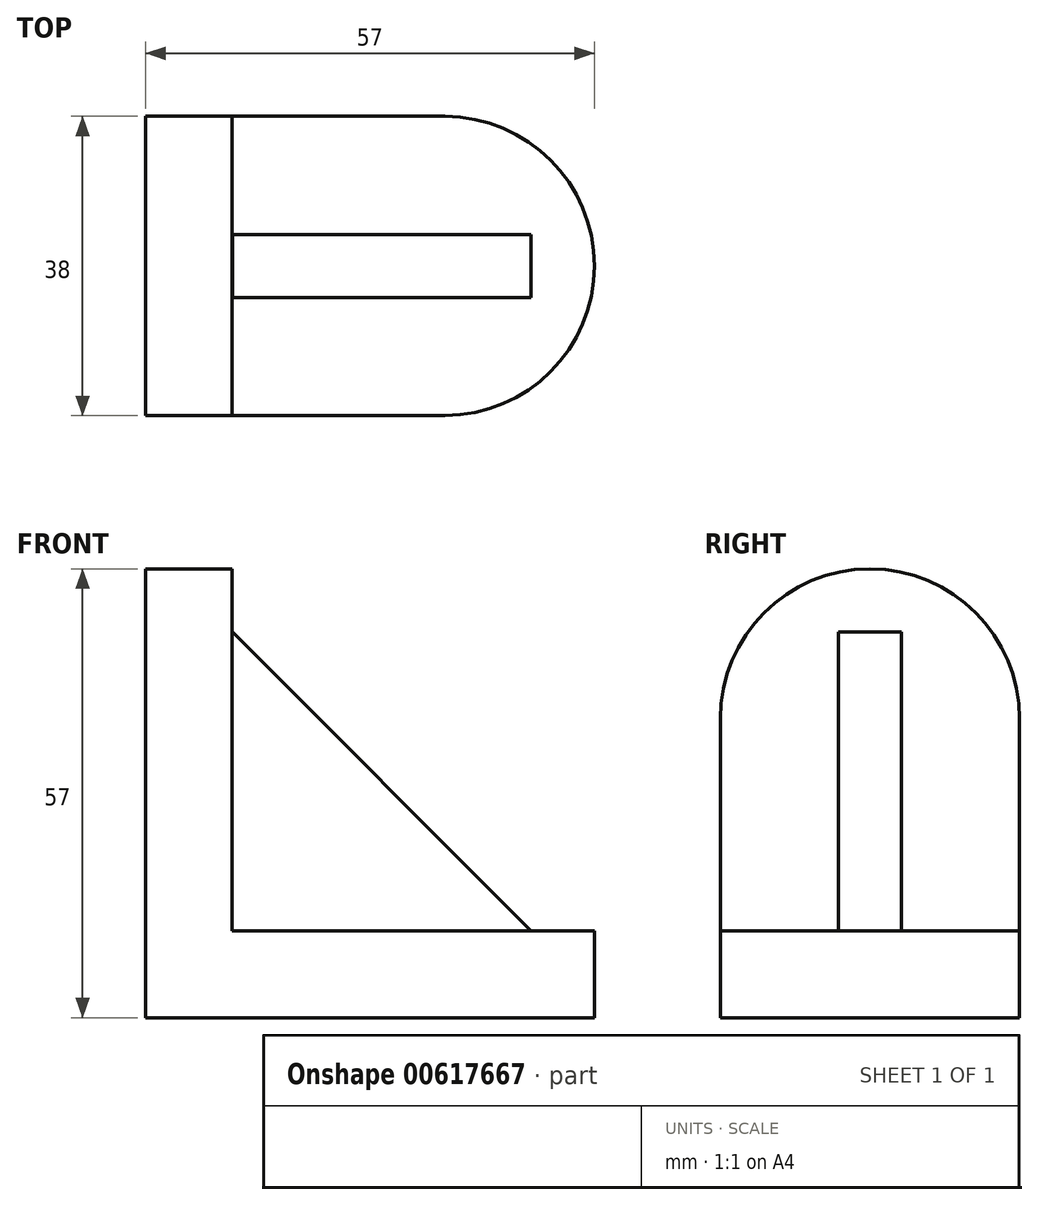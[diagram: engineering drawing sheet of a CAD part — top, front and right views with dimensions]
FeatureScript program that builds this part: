
annotation { "Feature Type Name" : "Feature", "Feature Type Description" : "" }
export const myFeature = defineFeature(function(context is Context, id is Id, definition is map)
    precondition{}
    {
        {
            var Q0;
            Q0=qCreatedBy(makeId("Top.planeOp"),FACE);
            var sketch = newSketch(context, id + "F0", { "sketchPlane" : qUnion([Q0])});
            skLineSegment(sketch, "E0", {"start": v(0, 0) * mm, "end": v(38, 0) * mm});
            skLineSegment(sketch, "E1", {"start": v(38, 38) * mm, "end": v(0, 38) * mm});
            skLineSegment(sketch, "E2", {"start": v(0, 38) * mm, "end": v(0, 0) * mm});
            skArc(sketch, "E3", {"start": v(38, 0) * mm, "mid": v(57, 19) * mm, "end": v(38, 38) * mm});
            skSolve(sketch);
        }
        {
            var Q0;
            Q0=qCreatedBy(makeId("Right.planeOp"),FACE);
            var sketch = newSketch(context, id + "F1", { "sketchPlane" : qUnion([Q0])});
            skLineSegment(sketch, "E4.bottom", {"start": v(0, 0) * mm, "end": v(38, 0) * mm});
            skLineSegment(sketch, "E4.top", {"start": v(0, 38) * mm, "end": v(38, 38) * mm});
            skLineSegment(sketch, "E4.left", {"start": v(0, 0) * mm, "end": v(0, 38) * mm});
            skLineSegment(sketch, "E4.right", {"start": v(38, 0) * mm, "end": v(38, 38) * mm});
            skArc(sketch, "E5", {"start": v(38, 38) * mm, "mid": v(19, 57) * mm, "end": v(0, 38) * mm});
            skSolve(sketch);
        }
        {
            var Q0;
            Q0=makeQuery(id+"F1.imprint","IMPRINT",FACE,{"disambiguationData":[TD([[makeQuery(id+"F1.imprint","IMPRINT",EDGE,{"derivedFrom":sQuery(id+"F1.wireOp",EDGE,"E4.bottom")}),1.0]])]});
            var Q1;
            Q1=makeQuery(id+"F1.imprint","IMPRINT",FACE,{"disambiguationData":[TD([[makeQuery(id+"F1.imprint","IMPRINT",EDGE,{"derivedFrom":sQuery(id+"F1.wireOp",EDGE,"E4.top")}),1.0]])]});
            extrude(context, id + "F2", {"entities" : qUnion([Q0, Q1]), "depth" : 11 * mm, "offsetDistance" : 25.4 * mm});
        }
        {
            var Q0;
            Q0=makeQuery(id+"F0.imprint","IMPRINT",FACE,{"disambiguationData":[TD([[makeQuery(id+"F0.imprint","IMPRINT",EDGE,{"derivedFrom":sQuery(id+"F0.wireOp",EDGE,"E0")}),1.0]])]});
            extrude(context, id + "F3", {"entities" : qUnion([Q0]), "operationType" : NewBodyOperationType.ADD, "depth" : 11 * mm, "offsetDistance" : 25.4 * mm});
        }
        {
            var Q0;
            Q0=makeQuery(id+"F3.opExtrude","CAP_EDGE",EDGE,{"disambiguationData":[OSD([sQuery(id+"F0.wireOp",EDGE,"E3")])],"isStart":false});
            cPoint(context, id + "F4", {"entities" : qUnion([Q0]), "parameter" : 0.5});
        }
        {
            var Q0;
            Q0=makeQuery(id+"F3.boolean.opBoolean","INTERSECT",EDGE,{"derivedFrom":[makeQuery(id+"F2.opExtrude","CAP_FACE",FACE,{"disambiguationData":[OSD([sQuery(id+"F1.wireOp",EDGE,"E4.bottom"),sQuery(id+"F1.wireOp",EDGE,"E4.left"),sQuery(id+"F1.wireOp",EDGE,"E4.right"),sQuery(id+"F1.wireOp",EDGE,"E5")])],"isStart":false}),makeQuery(id+"F3.opExtrude","CAP_FACE",FACE,{"disambiguationData":[OSD([sQuery(id+"F0.wireOp",EDGE,"E0"),sQuery(id+"F0.wireOp",EDGE,"E1"),sQuery(id+"F0.wireOp",EDGE,"E2"),sQuery(id+"F0.wireOp",EDGE,"E3")])],"isStart":false})]});
            cPoint(context, id + "F5", {"entities" : qUnion([Q0]), "parameter" : 0.5});
        }
        {
            var Q0;
            Q0=makeQuery(id+"F2.opExtrude","CAP_EDGE",EDGE,{"disambiguationData":[OSD([sQuery(id+"F1.wireOp",EDGE,"E5")])],"isStart":false});
            cPoint(context, id + "F6", {"entities" : qUnion([Q0]), "parameter" : 0.5});
        }
        {
            var Q0;
            Q0 = qCreatedBy(id + "F4" ,VERTEX);
            var Q1;
            Q1 = qCreatedBy(id + "F5" ,VERTEX);
            var Q2;
            Q2 = qCreatedBy(id + "F6" ,VERTEX);
            cPlane(context, id + "F7", {"entities" : qUnion([Q0, Q1, Q2]), "cplaneType" : CPlaneType.THREE_POINT, "offset" : 25.4 * mm, "width" : 152.4 * mm, "height" : 152.4 * mm});
        }
        {
            var Q0;
            Q0=qCreatedBy(id+"F7.planeOp",FACE);
            var sketch = newSketch(context, id + "F8", { "sketchPlane" : qUnion([Q0])});
            skPoint(sketch, "E6", {"position": v(49, 10.98) * mm});
            skPoint(sketch, "E7", {"position": v(11.04, 49) * mm});
            skLineSegment(sketch, "E8", {"start": v(11.04, 49) * mm, "end": v(49, 10.98) * mm});
            skSolve(sketch);
        }
        {
            var Q0;
            Q0=sQuery(id+"F8.wireOp",EDGE,"E8");
            extrude(context, id + "F9", {"bodyType" : ToolBodyType.SURFACE, "surfaceEntities" : qUnion([Q0]), "endBound" : BoundingType.SYMMETRIC, "depth" : 8 * mm, "offsetDistance" : 25.4 * mm});
        }
        {
            var Q0;
            Q0=makeQuery(id+"F9.opExtrude","SWEPT_FACE",FACE,{"disambiguationData":[OSD([sQuery(id+"F8.wireOp",EDGE,"E8")])]});
            var Q1;
            Q1=makeQuery(id+"F2.opExtrude","SWEPT_BODY",BODY,{"disambiguationData":[OSD([sQuery(id+"F1.wireOp",EDGE,"E4.bottom"),sQuery(id+"F1.wireOp",EDGE,"E4.left"),sQuery(id+"F1.wireOp",EDGE,"E4.right"),sQuery(id+"F1.wireOp",EDGE,"E5")])]});
            extrude(context, id + "F10", {"entities" : qUnion([Q0]), "operationType" : NewBodyOperationType.ADD, "endBound" : BoundingType.UP_TO_BODY, "depth" : 25.4 * mm, "endBoundEntityBody" : qUnion([Q1]), "offsetDistance" : 25.4 * mm});
        }
    });
